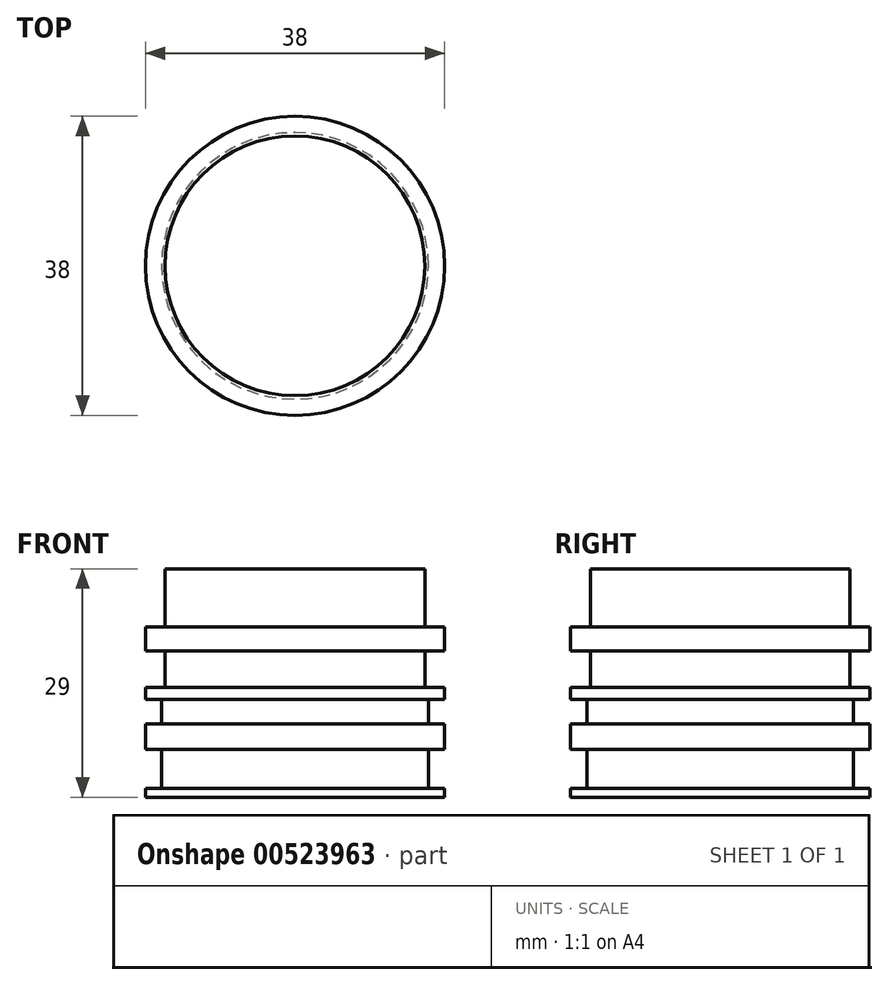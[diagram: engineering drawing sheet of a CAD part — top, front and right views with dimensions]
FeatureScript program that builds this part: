
annotation { "Feature Type Name" : "Feature", "Feature Type Description" : "" }
export const myFeature = defineFeature(function(context is Context, id is Id, definition is map)
    precondition{}
    {
        {
            var Q0;
            Q0=qCreatedBy(makeId("Top.planeOp"),FACE);
            var sketch = newSketch(context, id + "F0", { "sketchPlane" : qUnion([Q0])});
            skCircle(sketch, "E0", {"center": v(0, 0) * mm, "radius": 19 * mm});
            skSolve(sketch);
        }
        {
            var Q0;
            Q0 = qSketchRegion(id + "F0", true);
            extrude(context, id + "F1", {"entities" : qUnion([Q0]), "depth" : 29 * mm, "offsetDistance" : 25 * mm});
        }
        {
            var Q0;
            Q0=qCreatedBy(makeId("Front.planeOp"),FACE);
            var sketch = newSketch(context, id + "F2", { "sketchPlane" : qUnion([Q0])});
            skLineSegment(sketch, "E1.bottom", {"start": v(16.95, 1.1) * mm, "end": v(30, 1.1) * mm});
            skLineSegment(sketch, "E1.top", {"start": v(16.95, 6.1) * mm, "end": v(30, 6.1) * mm});
            skLineSegment(sketch, "E1.left", {"start": v(16.95, 1.1) * mm, "end": v(16.95, 6.1) * mm});
            skLineSegment(sketch, "E1.right", {"start": v(30, 1.1) * mm, "end": v(30, 6.1) * mm});
            skPoint(sketch, "E1.middle", {"position": v(23.47, 3.6) * mm});
            skLineSegment(sketch, "E2.bottom", {"start": v(16.95, 9.3) * mm, "end": v(30, 9.3) * mm});
            skLineSegment(sketch, "E2.top", {"start": v(16.95, 12.42) * mm, "end": v(30, 12.42) * mm});
            skLineSegment(sketch, "E2.left", {"start": v(16.94, 9.3) * mm, "end": v(16.94, 12.42) * mm});
            skLineSegment(sketch, "E2.right", {"start": v(30, 9.3) * mm, "end": v(30, 12.42) * mm});
            skPoint(sketch, "E2.middle", {"position": v(23.47, 10.86) * mm});
            skLineSegment(sketch, "E3.bottom", {"start": v(16.5, 13.92) * mm, "end": v(30, 13.92) * mm});
            skLineSegment(sketch, "E3.top", {"start": v(16.5, 18.6) * mm, "end": v(30, 18.6) * mm});
            skLineSegment(sketch, "E3.left", {"start": v(16.5, 13.92) * mm, "end": v(16.5, 18.6) * mm});
            skLineSegment(sketch, "E3.right", {"start": v(30, 13.92) * mm, "end": v(30, 18.6) * mm});
            skPoint(sketch, "E3.middle", {"position": v(23.25, 16.25) * mm});
            skLineSegment(sketch, "E4", {"start": v(0, 21.1) * mm, "end": v(0, -3.44) * mm, "construction": true});
            skLineSegment(sketch, "E5", {"start": v(0, -3.44) * mm, "end": v(0, -1.86) * mm, "construction": true});
            skLineSegment(sketch, "E6.bottom", {"start": v(16.5, 21.66) * mm, "end": v(30.4, 21.66) * mm});
            skLineSegment(sketch, "E6.top", {"start": v(16.5, 31.66) * mm, "end": v(30.4, 31.66) * mm});
            skLineSegment(sketch, "E6.left", {"start": v(16.5, 21.66) * mm, "end": v(16.5, 31.66) * mm});
            skLineSegment(sketch, "E6.right", {"start": v(30.4, 21.66) * mm, "end": v(30.4, 31.66) * mm});
            skPoint(sketch, "E6.middle", {"position": v(23.45, 26.66) * mm});
            skSolve(sketch);
        }
        {
            var Q0;
            Q0 = qSketchRegion(id + "F2", true);
            var Q1;
            Q1=sQuery(id+"F2.wireOp",EDGE,"E4");
            revolve(context, id + "F3", {"operationType" : NewBodyOperationType.REMOVE, "entities" : qUnion([Q0]), "axis" : qUnion([Q1]), "revolveType" : RevolveType.FULL, "oppositeDirection" : true});
        }
    });
